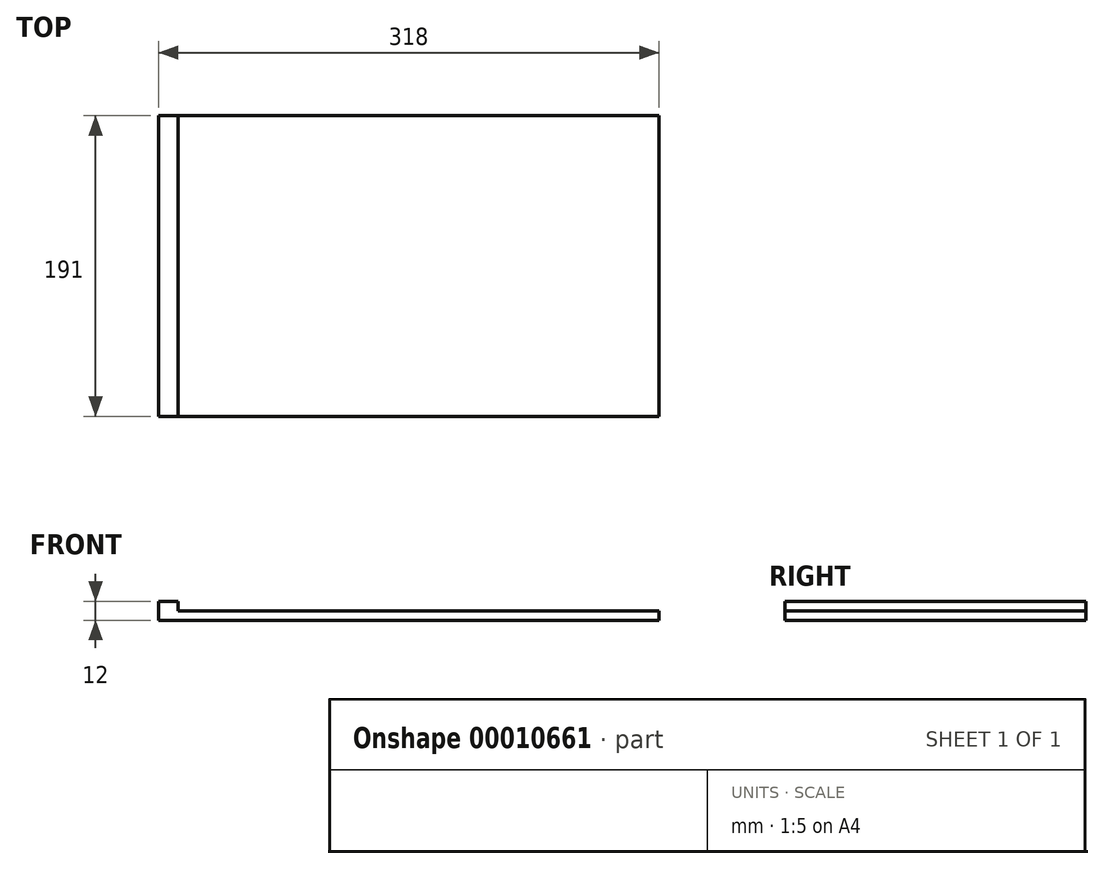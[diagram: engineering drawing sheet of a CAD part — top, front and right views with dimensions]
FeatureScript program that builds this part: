
annotation { "Feature Type Name" : "Feature", "Feature Type Description" : "" }
export const myFeature = defineFeature(function(context is Context, id is Id, definition is map)
    precondition{}
    {
        {
            var Q0;
            Q0=qCreatedBy(makeId("Top.planeOp"),FACE);
            var sketch = newSketch(context, id + "F0", { "sketchPlane" : qUnion([Q0])});
            skLineSegment(sketch, "E0.bottom", {"start": v(0, 0) * mm, "end": v(318, 0) * mm});
            skLineSegment(sketch, "E0.top", {"start": v(0, 191) * mm, "end": v(318, 191) * mm});
            skLineSegment(sketch, "E0.left", {"start": v(0, 0) * mm, "end": v(0, 191) * mm});
            skLineSegment(sketch, "E0.right", {"start": v(318, 0) * mm, "end": v(318, 191) * mm});
            skSolve(sketch);
        }
        {
            var Q0;
            Q0=makeQuery(id+"F0.imprint","IMPRINT",FACE,{"disambiguationData":[TD([[makeQuery(id+"F0.imprint","IMPRINT",EDGE,{"derivedFrom":sQuery(id+"F0.wireOp",EDGE,"E0.bottom")}),1.0]])]});
            extrude(context, id + "F1", {"entities" : qUnion([Q0]), "depth" : 6 * mm});
        }
        {
            var Q0;
            Q0=makeQuery(id+"F1.opExtrude","CAP_FACE",FACE,{"disambiguationData":[OSD([sQuery(id+"F0.wireOp",EDGE,"E0.bottom"),sQuery(id+"F0.wireOp",EDGE,"E0.top"),sQuery(id+"F0.wireOp",EDGE,"E0.left"),sQuery(id+"F0.wireOp",EDGE,"E0.right")])],"isStart":false});
            var sketch = newSketch(context, id + "F2", { "sketchPlane" : qUnion([Q0])});
            skLineSegment(sketch, "E1.bottom", {"start": v(0, 191) * mm, "end": v(12.43, 191) * mm});
            skLineSegment(sketch, "E1.top", {"start": v(0, 0) * mm, "end": v(12.43, 0) * mm});
            skLineSegment(sketch, "E1.left", {"start": v(0, 191) * mm, "end": v(0, 0) * mm});
            skLineSegment(sketch, "E1.right", {"start": v(12.43, 191) * mm, "end": v(12.43, 0) * mm});
            skLineSegment(sketch, "E2.bottom", {"start": v(83.98, -30.9) * mm, "end": v(83.98, -30.9) * mm});
            skLineSegment(sketch, "E2.top", {"start": v(83.98, -19.39) * mm, "end": v(83.98, -19.39) * mm});
            skLineSegment(sketch, "E2.left", {"start": v(83.98, -30.9) * mm, "end": v(83.98, -19.39) * mm});
            skLineSegment(sketch, "E2.right", {"start": v(83.98, -30.9) * mm, "end": v(83.98, -19.39) * mm});
            skSolve(sketch);
        }
        {
            var Q0;
            Q0=makeQuery(id+"F2.imprint","IMPRINT",FACE,{"disambiguationData":[TD([[makeQuery(id+"F2.imprint","IMPRINT",EDGE,{"derivedFrom":sQuery(id+"F2.wireOp",EDGE,"E1.bottom")}),-1.0]])]});
            extrude(context, id + "F3", {"entities" : qUnion([Q0]), "operationType" : NewBodyOperationType.ADD, "depth" : 6 * mm});
        }
    });
